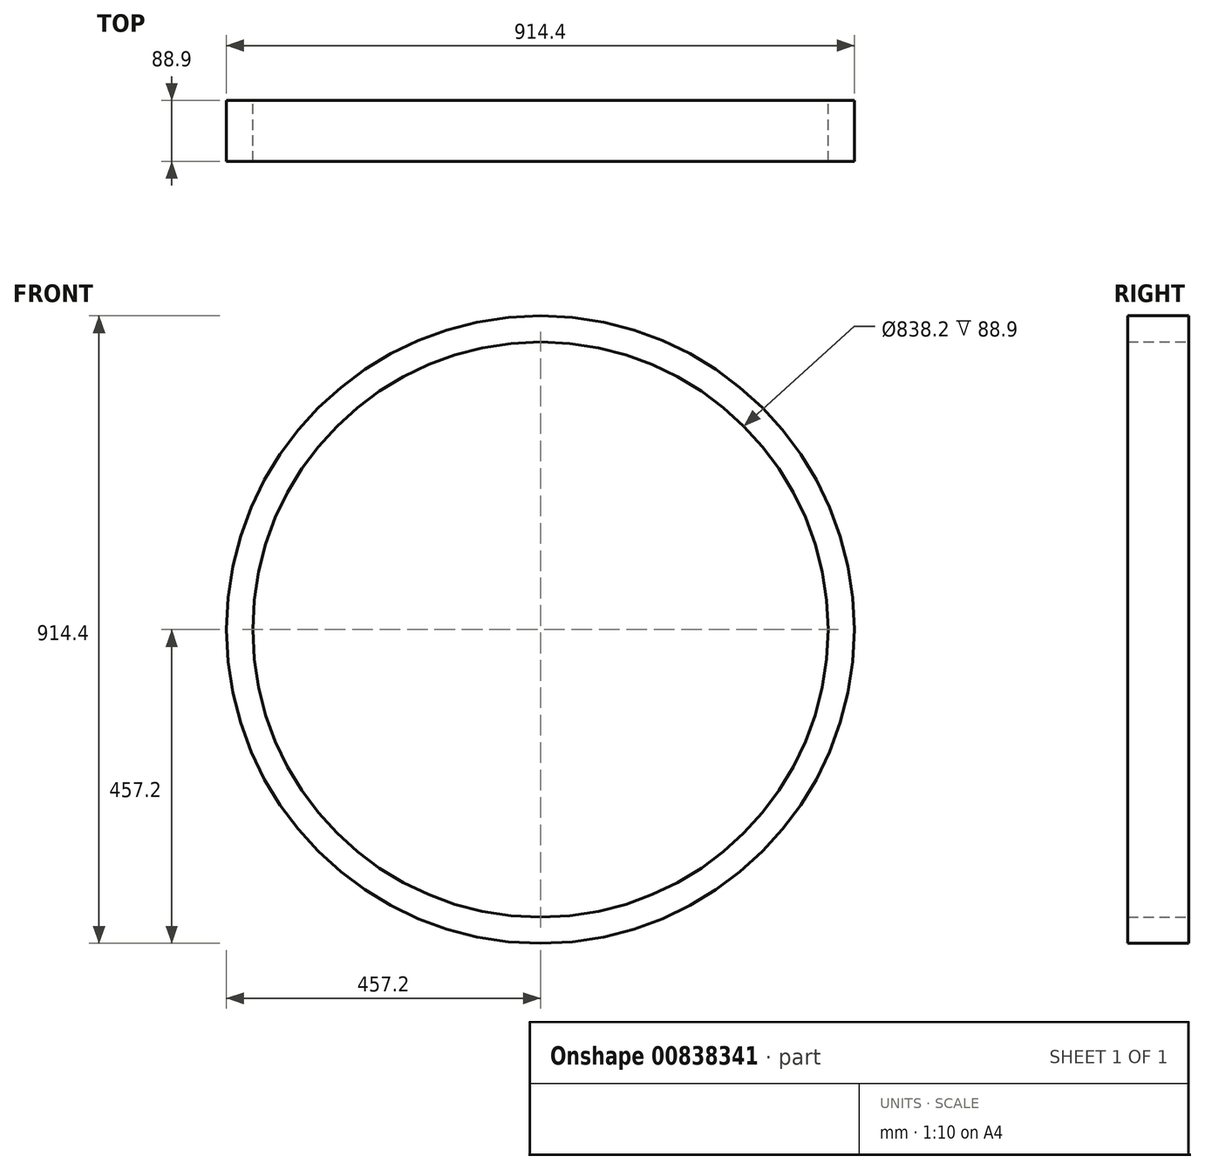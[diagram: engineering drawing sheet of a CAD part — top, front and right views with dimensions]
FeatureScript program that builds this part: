
annotation { "Feature Type Name" : "Feature", "Feature Type Description" : "" }
export const myFeature = defineFeature(function(context is Context, id is Id, definition is map)
    precondition{}
    {
        {
            var Q0;
            Q0=qCreatedBy(makeId("Front.planeOp"),FACE);
            var sketch = newSketch(context, id + "F0", { "sketchPlane" : qUnion([Q0])});
            skCircle(sketch, "E0", {"center": v(0, 0) * mm, "radius": 457.2 * mm});
            skCircle(sketch, "E1.0", {"center": v(0, 0) * mm, "radius": 419.1 * mm});
            skSolve(sketch);
        }
        {
            var Q0;
            Q0 = qSketchRegion(id + "F0", true);
            extrude(context, id + "F1", {"entities" : qUnion([Q0]), "depth" : 88.9 * mm, "offsetDistance" : 25.4 * mm});
        }
    });
